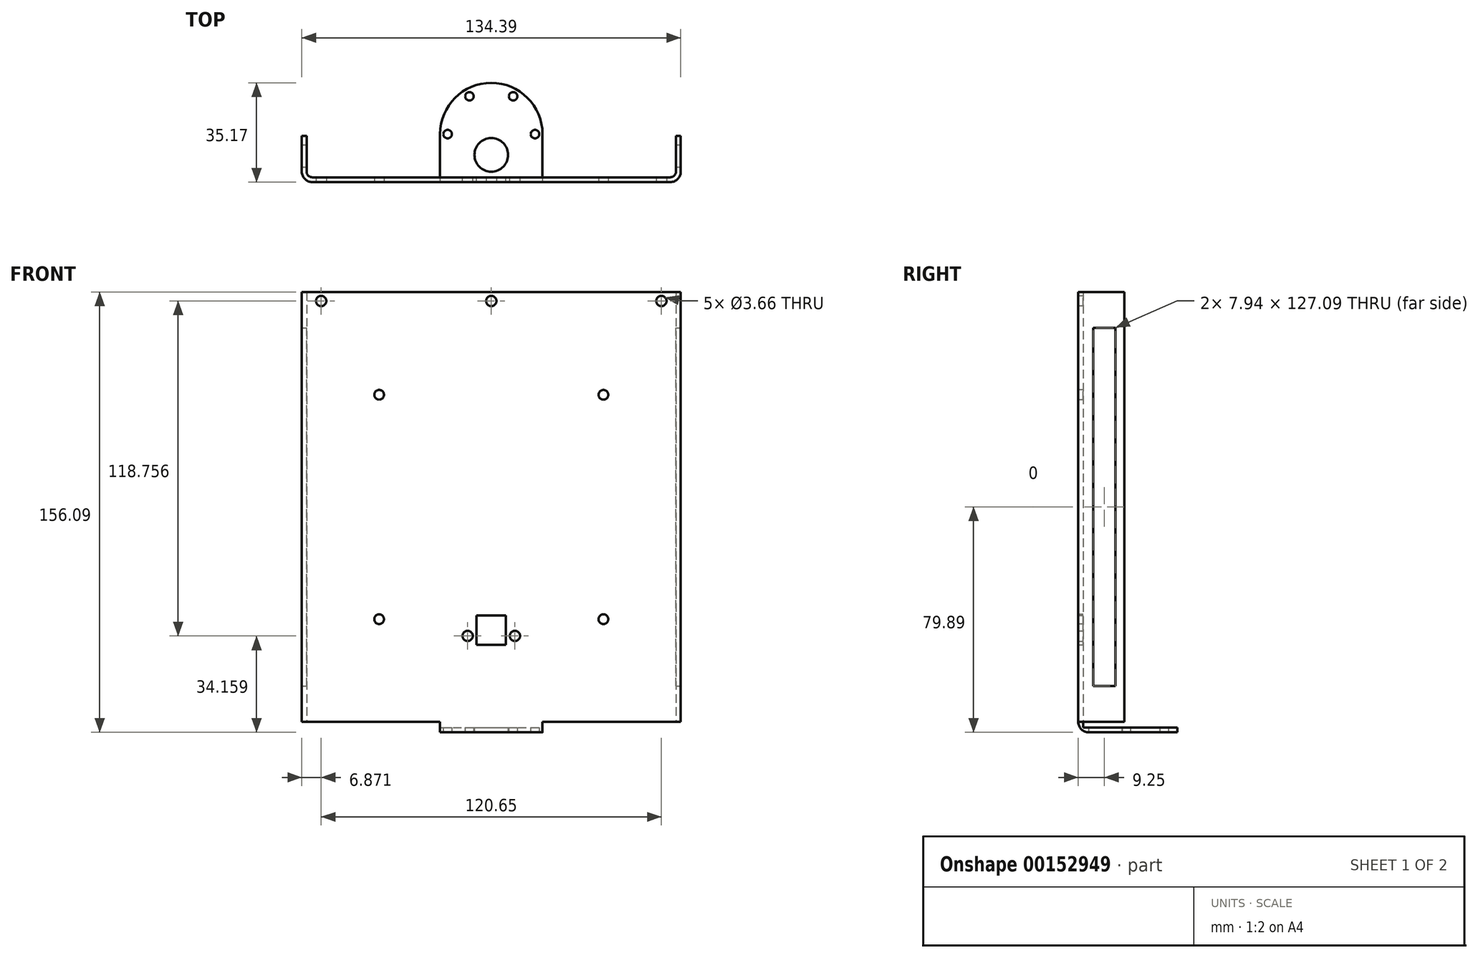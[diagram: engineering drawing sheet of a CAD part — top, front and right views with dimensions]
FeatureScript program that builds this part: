
annotation { "Feature Type Name" : "Feature", "Feature Type Description" : "" }
export const myFeature = defineFeature(function(context is Context, id is Id, definition is map)
    precondition{}
    {
        {
            var Q0;
            Q0=qCreatedBy(makeId("Top.planeOp"),FACE);
            var sketch = newSketch(context, id + "F0", { "sketchPlane" : qUnion([Q0])});
            skLineSegment(sketch, "E0.bottom", {"start": v(0, 0) * mm, "end": v(-130.97, 0) * mm});
            skLineSegment(sketch, "E0.top", {"start": v(1.7, -1.7) * mm, "end": v(-132.68, -1.7) * mm});
            skLineSegment(sketch, "E1.top", {"start": v(-130.97, 14.68) * mm, "end": v(-132.68, 14.68) * mm});
            skLineSegment(sketch, "E1.left", {"start": v(-130.97, 0) * mm, "end": v(-130.97, 14.68) * mm});
            skLineSegment(sketch, "E1.right", {"start": v(-132.68, -1.7) * mm, "end": v(-132.68, 14.68) * mm});
            skLineSegment(sketch, "E2.top", {"start": v(0, 14.68) * mm, "end": v(1.7, 14.68) * mm});
            skLineSegment(sketch, "E2.left", {"start": v(0, 0) * mm, "end": v(0, 14.68) * mm});
            skLineSegment(sketch, "E2.right", {"start": v(1.7, -1.7) * mm, "end": v(1.7, 14.68) * mm});
            skLineSegment(sketch, "E3", {"start": v(-65.48, 0) * mm, "end": v(-65.48, -1.7) * mm, "construction": true});
            skSolve(sketch);
        }
        {
            var Q0;
            Q0=qSketchRegion(id+"F0",true);
            extrude(context, id + "F1", {"entities" : qUnion([Q0]), "depth" : 152.4 * mm});
        }
        {
            var Q0;
            Q0=makeQuery(id+"F1.opExtrude","SWEPT_FACE",FACE,{"disambiguationData":[OSD([sQuery(id+"F0.wireOp",EDGE,"E2.right")])]});
            var sketch = newSketch(context, id + "F2", { "sketchPlane" : qUnion([Q0])});
            skLineSegment(sketch, "E4.bottom", {"start": v(11.5, 139.75) * mm, "end": v(3.57, 139.75) * mm});
            skLineSegment(sketch, "E4.top", {"start": v(11.5, 12.65) * mm, "end": v(3.57, 12.65) * mm});
            skLineSegment(sketch, "E4.left", {"start": v(11.5, 139.75) * mm, "end": v(11.5, 12.65) * mm});
            skLineSegment(sketch, "E4.right", {"start": v(3.57, 139.75) * mm, "end": v(3.57, 12.65) * mm});
            skLineSegment(sketch, "E5", {"start": v(11.5, 76.2) * mm, "end": v(14.68, 76.2) * mm, "construction": true});
            skSolve(sketch);
        }
        {
            var Q0;
            Q0 = qSketchRegion(id + "F2", true);
            var Q1;
            Q1=makeQuery(id+"F1.opExtrude","SWEPT_FACE",FACE,{"disambiguationData":[OSD([sQuery(id+"F0.wireOp",EDGE,"E1.right")])]});
            extrude(context, id + "F3", {"entities" : qUnion([Q0]), "operationType" : NewBodyOperationType.REMOVE, "endBound" : BoundingType.UP_TO_SURFACE, "oppositeDirection" : true, "endBoundEntityFace" : qUnion([Q1]), "depth" : 25.4 * mm});
        }
        {
            var Q0;
            Q0=makeQuery(id+"F1.opExtrude","CAP_FACE",FACE,{"disambiguationData":[OSD([sQuery(id+"F0.wireOp",EDGE,"E0.bottom"),sQuery(id+"F0.wireOp",EDGE,"E0.top"),sQuery(id+"F0.wireOp",EDGE,"E1.top"),sQuery(id+"F0.wireOp",EDGE,"E1.left"),sQuery(id+"F0.wireOp",EDGE,"E1.right"),sQuery(id+"F0.wireOp",EDGE,"E2.top"),sQuery(id+"F0.wireOp",EDGE,"E2.left"),sQuery(id+"F0.wireOp",EDGE,"E2.right")])],"isStart":true});
            var sketch = newSketch(context, id + "F4", { "sketchPlane" : qUnion([Q0])});
            skLineSegment(sketch, "E6.bottom", {"start": v(-47.32, 0) * mm, "end": v(-83.64, 0) * mm});
            skLineSegment(sketch, "E6.top", {"start": v(-47.32, 1.7) * mm, "end": v(-83.64, 1.7) * mm});
            skLineSegment(sketch, "E6.left", {"start": v(-47.32, 0) * mm, "end": v(-47.32, 1.7) * mm});
            skLineSegment(sketch, "E6.right", {"start": v(-83.64, 0) * mm, "end": v(-83.64, 1.7) * mm});
            skPoint(sketch, "E7", {"position": v(-65.48, 1.7) * mm});
            skSolve(sketch);
        }
        {
            var Q0;
            Q0 = qSketchRegion(id + "F4", true);
            extrude(context, id + "F5", {"entities" : qUnion([Q0]), "operationType" : NewBodyOperationType.ADD, "depth" : 3.7 * mm});
        }
        {
            var Q0;
            Q0=makeQuery(id+"F5.boolean.opBoolean","MERGE",FACE,{"derivedFrom":[makeQuery(id+"F1.opExtrude","SWEPT_FACE",FACE,{"disambiguationData":[OSD([sQuery(id+"F0.wireOp",EDGE,"E0.bottom")])]}),makeQuery(id+"F5.opExtrude","SWEPT_FACE",FACE,{"disambiguationData":[OSD([sQuery(id+"F4.wireOp",EDGE,"E6.bottom")])]})]});
            var sketch = newSketch(context, id + "F6", { "sketchPlane" : qUnion([Q0])});
            skLineSegment(sketch, "E8.bottom", {"start": v(83.64, -3.7) * mm, "end": v(47.32, -3.7) * mm});
            skLineSegment(sketch, "E8.top", {"start": v(83.64, -1.98) * mm, "end": v(47.32, -1.98) * mm});
            skLineSegment(sketch, "E8.left", {"start": v(83.64, -3.7) * mm, "end": v(83.64, -1.98) * mm});
            skLineSegment(sketch, "E8.right", {"start": v(47.32, -3.7) * mm, "end": v(47.32, -1.98) * mm});
            skSolve(sketch);
        }
        {
            var Q0;
            Q0 = qSketchRegion(id + "F6", true);
            extrude(context, id + "F7", {"entities" : qUnion([Q0]), "operationType" : NewBodyOperationType.ADD, "depth" : 33.46 * mm});
        }
        {
            var Q0;
            Q0=makeQuery(id+"F1.opExtrude","SWEPT_EDGE",EDGE,{"disambiguationData":[OSD([sQuery(id+"F0.wireOp",EDGE,"E0.top"),sQuery(id+"F0.wireOp",EDGE,"E2.right")])]});
            var Q1;
            Q1=makeQuery(id+"F1.opExtrude","SWEPT_EDGE",EDGE,{"disambiguationData":[OSD([sQuery(id+"F0.wireOp",EDGE,"E0.top"),sQuery(id+"F0.wireOp",EDGE,"E1.right")])]});
            var Q2;
            Q2=makeQuery(id+"F5.opExtrude","CAP_EDGE",EDGE,{"disambiguationData":[OSD([sQuery(id+"F4.wireOp",EDGE,"E6.top")])],"isStart":false});
            fillet(context, id + "F8", {"entities" : qUnion([Q0, Q1, Q2]), "radius" : 3.7 * mm, "tangentPropagation" : true, "allowEdgeOverflow" : false});
        }
        {
            var Q0;
            Q0=makeQuery(id+"F1.opExtrude","SWEPT_EDGE",EDGE,{"disambiguationData":[OSD([sQuery(id+"F0.wireOp",EDGE,"E0.bottom"),sQuery(id+"F0.wireOp",EDGE,"E2.left")])]});
            var Q1;
            Q1=makeQuery(id+"F1.opExtrude","SWEPT_EDGE",EDGE,{"disambiguationData":[OSD([sQuery(id+"F0.wireOp",EDGE,"E0.bottom"),sQuery(id+"F0.wireOp",EDGE,"E1.left")])]});
            var Q2;
            Q2=makeQuery(id+"F7.opExtrude","CAP_EDGE",EDGE,{"disambiguationData":[OSD([sQuery(id+"F6.wireOp",EDGE,"E8.top")])],"isStart":true});
            fillet(context, id + "F9", {"entities" : qUnion([Q0, Q1, Q2]), "radius" : 1.98 * mm, "tangentPropagation" : true, "allowEdgeOverflow" : false});
        }
        {
            var Q0;
            Q0=makeQuery(id+"F7.boolean.opBoolean","MERGE",FACE,{"derivedFrom":[makeQuery(id+"F5.opExtrude","CAP_FACE",FACE,{"disambiguationData":[OSD([sQuery(id+"F4.wireOp",EDGE,"E6.bottom"),sQuery(id+"F4.wireOp",EDGE,"E6.top"),sQuery(id+"F4.wireOp",EDGE,"E6.left"),sQuery(id+"F4.wireOp",EDGE,"E6.right")])],"isStart":false}),makeQuery(id+"F7.opExtrude","SWEPT_FACE",FACE,{"disambiguationData":[OSD([sQuery(id+"F6.wireOp",EDGE,"E8.bottom")])]})]});
            var sketch = newSketch(context, id + "F10", { "sketchPlane" : qUnion([Q0])});
            skLineSegment(sketch, "E9", {"start": v(-65.48, -15.3) * mm, "end": v(-65.48, -7.94) * mm, "construction": true});
            skCircle(sketch, "E10.cCircle", {"center": v(-65.48, -15.3) * mm, "radius": 13.42 * mm, "construction": true});
            skLineSegment(sketch, "E10.0", {"start": v(-73.23, -1.89) * mm, "end": v(-57.74, -1.89) * mm, "construction": true});
            skLineSegment(sketch, "E10.1", {"start": v(-57.74, -1.89) * mm, "end": v(-49.99, -15.3) * mm, "construction": true});
            skLineSegment(sketch, "E10.2", {"start": v(-49.99, -15.3) * mm, "end": v(-57.74, -28.72) * mm, "construction": true});
            skLineSegment(sketch, "E10.3", {"start": v(-57.74, -28.72) * mm, "end": v(-73.23, -28.72) * mm, "construction": true});
            skLineSegment(sketch, "E10.4", {"start": v(-73.23, -28.72) * mm, "end": v(-80.98, -15.3) * mm, "construction": true});
            skLineSegment(sketch, "E10.5", {"start": v(-80.98, -15.3) * mm, "end": v(-73.23, -1.89) * mm, "construction": true});
            skPoint(sketch, "E10.0.midPoint", {"position": v(-65.48, -1.89) * mm});
            skCircle(sketch, "E11", {"center": v(-65.48, -7.94) * mm, "radius": 5.97 * mm});
            skCircle(sketch, "E12", {"center": v(-49.99, -15.3) * mm, "radius": 1.5 * mm});
            skCircle(sketch, "E13", {"center": v(-80.98, -15.3) * mm, "radius": 1.5 * mm});
            skCircle(sketch, "E14", {"center": v(-73.23, -28.72) * mm, "radius": 1.5 * mm});
            skCircle(sketch, "E15", {"center": v(-57.74, -28.72) * mm, "radius": 1.5 * mm});
            skLineSegment(sketch, "E16", {"start": v(-65.48, -15.3) * mm, "end": v(-65.48, -33.46) * mm, "construction": true});
            skSolve(sketch);
        }
        {
            var Q0;
            Q0 = qSketchRegion(id + "F10", true);
            var Q1;
            {var subQ0=sQuery(id+"F0.wireOp",EDGE,"E2.top");var subQ1=sQuery(id+"F0.wireOp",EDGE,"E2.left");var subQ2=sQuery(id+"F0.wireOp",EDGE,"E0.top");var subQ3=sQuery(id+"F0.wireOp",EDGE,"E0.bottom");var subQ4=sQuery(id+"F0.wireOp",EDGE,"E2.right");Q1=makeQuery(id+"F5.boolean.opBoolean","SPLIT",FACE,{"disambiguationData":[TD([makeQuery(id+"F1.opExtrude","SWEPT_FACE",FACE,{"disambiguationData":[OSD([subQ0])]})])],"derivedFrom":makeQuery(id+"F1.opExtrude","CAP_FACE",FACE,{"disambiguationData":[OSD([subQ3,subQ2,sQuery(id+"F0.wireOp",EDGE,"E1.top"),sQuery(id+"F0.wireOp",EDGE,"E1.left"),sQuery(id+"F0.wireOp",EDGE,"E1.right"),subQ0,subQ1,subQ4])],"isStart":true})});}
            extrude(context, id + "F11", {"entities" : qUnion([Q0]), "operationType" : NewBodyOperationType.REMOVE, "endBound" : BoundingType.UP_TO_SURFACE, "oppositeDirection" : true, "endBoundEntityFace" : qUnion([Q1]), "depth" : 25.4 * mm});
        }
        {
            var Q0;
            Q0=makeQuery(id+"F7.opExtrude","CAP_EDGE",EDGE,{"disambiguationData":[OSD([sQuery(id+"F6.wireOp",EDGE,"E8.right")])],"isStart":false});
            var Q1;
            Q1=makeQuery(id+"F7.opExtrude","CAP_EDGE",EDGE,{"disambiguationData":[OSD([sQuery(id+"F6.wireOp",EDGE,"E8.left")])],"isStart":false});
            fillet(context, id + "F12", {"entities" : qUnion([Q0, Q1]), "radius" : 18.16 * mm, "tangentPropagation" : true, "allowEdgeOverflow" : false});
        }
        {
            var Q0;
            Q0=makeQuery(id+"F5.boolean.opBoolean","MERGE",FACE,{"derivedFrom":[makeQuery(id+"F1.opExtrude","SWEPT_FACE",FACE,{"disambiguationData":[OSD([sQuery(id+"F0.wireOp",EDGE,"E0.top")])]}),makeQuery(id+"F5.opExtrude","SWEPT_FACE",FACE,{"disambiguationData":[OSD([sQuery(id+"F4.wireOp",EDGE,"E6.top")])]})]});
            var sketch = newSketch(context, id + "F13", { "sketchPlane" : qUnion([Q0])});
            skLineSegment(sketch, "E17", {"start": v(-65.48, 152.4) * mm, "end": v(-65.48, 149.22) * mm, "construction": true});
            skLineSegment(sketch, "E18", {"start": v(-128.98, 149.22) * mm, "end": v(-125.8, 149.22) * mm, "construction": true});
            skLineSegment(sketch, "E19", {"start": v(-125.8, 149.22) * mm, "end": v(-5.16, 149.22) * mm, "construction": true});
            skLineSegment(sketch, "E20", {"start": v(-5.16, 149.22) * mm, "end": v(-1.98, 149.22) * mm, "construction": true});
            skCircle(sketch, "E21", {"center": v(-65.48, 149.22) * mm, "radius": 1.83 * mm});
            skCircle(sketch, "E22", {"center": v(-5.16, 149.22) * mm, "radius": 1.83 * mm});
            skCircle(sketch, "E23", {"center": v(-125.8, 149.22) * mm, "radius": 1.83 * mm});
            skSolve(sketch);
        }
        {
            var Q0;
            Q0 = qSketchRegion(id + "F13", true);
            var Q1;
            Q1=makeQuery(id+"F5.boolean.opBoolean","MERGE",FACE,{"derivedFrom":[makeQuery(id+"F1.opExtrude","SWEPT_FACE",FACE,{"disambiguationData":[OSD([sQuery(id+"F0.wireOp",EDGE,"E0.bottom")])]}),makeQuery(id+"F5.opExtrude","SWEPT_FACE",FACE,{"disambiguationData":[OSD([sQuery(id+"F4.wireOp",EDGE,"E6.bottom")])]})]});
            extrude(context, id + "F14", {"entities" : qUnion([Q0]), "operationType" : NewBodyOperationType.REMOVE, "endBound" : BoundingType.UP_TO_SURFACE, "oppositeDirection" : true, "endBoundEntityFace" : qUnion([Q1]), "depth" : 25.4 * mm});
        }
        {
            var Q0;
            Q0=makeQuery(id+"F5.boolean.opBoolean","MERGE",FACE,{"derivedFrom":[makeQuery(id+"F1.opExtrude","SWEPT_FACE",FACE,{"disambiguationData":[OSD([sQuery(id+"F0.wireOp",EDGE,"E0.top")])]}),makeQuery(id+"F5.opExtrude","SWEPT_FACE",FACE,{"disambiguationData":[OSD([sQuery(id+"F4.wireOp",EDGE,"E6.top")])]})]});
            var sketch = newSketch(context, id + "F15", { "sketchPlane" : qUnion([Q0])});
            skLineSegment(sketch, "E24", {"start": v(-128.98, 76.2) * mm, "end": v(-1.98, 76.2) * mm, "construction": true});
            skLineSegment(sketch, "E25.bottom", {"start": v(-25.7, 36.43) * mm, "end": v(-105.26, 36.43) * mm, "construction": true});
            skLineSegment(sketch, "E25.top", {"start": v(-25.7, 115.97) * mm, "end": v(-105.26, 115.97) * mm, "construction": true});
            skLineSegment(sketch, "E25.left", {"start": v(-25.7, 36.43) * mm, "end": v(-25.7, 115.97) * mm, "construction": true});
            skLineSegment(sketch, "E25.right", {"start": v(-105.26, 36.43) * mm, "end": v(-105.26, 115.97) * mm, "construction": true});
            skPoint(sketch, "E25.middle", {"position": v(-65.48, 76.2) * mm});
            skCircle(sketch, "E26", {"center": v(-105.26, 115.97) * mm, "radius": 1.73 * mm});
            skCircle(sketch, "E27", {"center": v(-25.7, 115.97) * mm, "radius": 1.73 * mm});
            skCircle(sketch, "E28", {"center": v(-25.7, 36.43) * mm, "radius": 1.73 * mm});
            skCircle(sketch, "E29", {"center": v(-105.26, 36.43) * mm, "radius": 1.73 * mm});
            skSolve(sketch);
        }
        {
            var Q0;
            Q0 = qSketchRegion(id + "F15", true);
            var Q1;
            Q1=makeQuery(id+"F5.boolean.opBoolean","MERGE",FACE,{"derivedFrom":[makeQuery(id+"F1.opExtrude","SWEPT_FACE",FACE,{"disambiguationData":[OSD([sQuery(id+"F0.wireOp",EDGE,"E0.bottom")])]}),makeQuery(id+"F5.opExtrude","SWEPT_FACE",FACE,{"disambiguationData":[OSD([sQuery(id+"F4.wireOp",EDGE,"E6.bottom")])]})]});
            extrude(context, id + "F16", {"entities" : qUnion([Q0]), "operationType" : NewBodyOperationType.REMOVE, "endBound" : BoundingType.UP_TO_SURFACE, "oppositeDirection" : true, "endBoundEntityFace" : qUnion([Q1]), "depth" : 25.4 * mm});
        }
        {
            var Q0;
            Q0=makeQuery(id+"F5.boolean.opBoolean","MERGE",FACE,{"derivedFrom":[makeQuery(id+"F1.opExtrude","SWEPT_FACE",FACE,{"disambiguationData":[OSD([sQuery(id+"F0.wireOp",EDGE,"E0.bottom")])]}),makeQuery(id+"F5.opExtrude","SWEPT_FACE",FACE,{"disambiguationData":[OSD([sQuery(id+"F4.wireOp",EDGE,"E6.bottom")])]})]});
            var sketch = newSketch(context, id + "F17", { "sketchPlane" : qUnion([Q0])});
            skLineSegment(sketch, "E30", {"start": v(65.48, -1.98) * mm, "end": v(65.48, 27.3) * mm, "construction": true});
            skLineSegment(sketch, "E31.bottom", {"start": v(70.69, 27.3) * mm, "end": v(60.28, 27.3) * mm});
            skLineSegment(sketch, "E31.top", {"start": v(70.69, 37.7) * mm, "end": v(60.28, 37.7) * mm});
            skLineSegment(sketch, "E31.left", {"start": v(70.69, 27.3) * mm, "end": v(70.69, 37.7) * mm});
            skLineSegment(sketch, "E31.right", {"start": v(60.28, 27.3) * mm, "end": v(60.28, 37.7) * mm});
            skLineSegment(sketch, "E32", {"start": v(60.28, 27.3) * mm, "end": v(57.1, 27.3) * mm, "construction": true});
            skLineSegment(sketch, "E33", {"start": v(57.1, 27.3) * mm, "end": v(57.1, 30.47) * mm, "construction": true});
            skLineSegment(sketch, "E34", {"start": v(70.69, 27.3) * mm, "end": v(73.86, 27.3) * mm, "construction": true});
            skLineSegment(sketch, "E35", {"start": v(73.86, 27.3) * mm, "end": v(73.86, 30.47) * mm, "construction": true});
            skCircle(sketch, "E36", {"center": v(73.86, 30.47) * mm, "radius": 1.83 * mm});
            skCircle(sketch, "E37", {"center": v(57.1, 30.47) * mm, "radius": 1.83 * mm});
            skSolve(sketch);
        }
        {
            var Q0;
            Q0 = qSketchRegion(id + "F17", true);
            var Q1;
            Q1=makeQuery(id+"F5.boolean.opBoolean","MERGE",FACE,{"derivedFrom":[makeQuery(id+"F1.opExtrude","SWEPT_FACE",FACE,{"disambiguationData":[OSD([sQuery(id+"F0.wireOp",EDGE,"E0.top")])]}),makeQuery(id+"F5.opExtrude","SWEPT_FACE",FACE,{"disambiguationData":[OSD([sQuery(id+"F4.wireOp",EDGE,"E6.top")])]})]});
            extrude(context, id + "F18", {"entities" : qUnion([Q0]), "operationType" : NewBodyOperationType.REMOVE, "endBound" : BoundingType.UP_TO_SURFACE, "oppositeDirection" : true, "endBoundEntityFace" : qUnion([Q1]), "depth" : 25.4 * mm});
        }
    });
